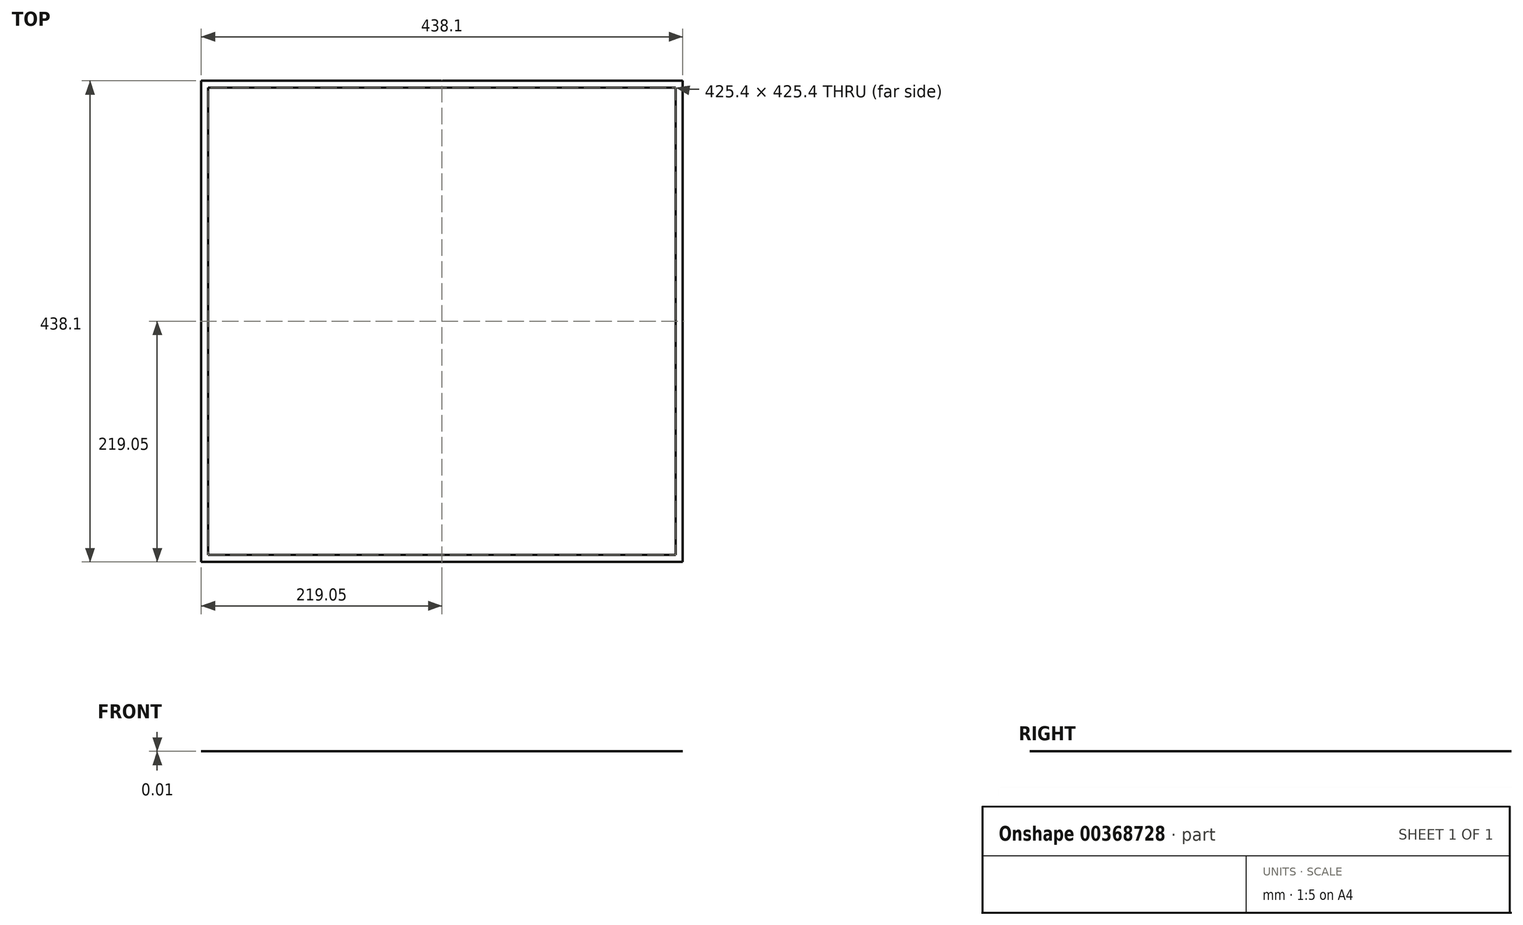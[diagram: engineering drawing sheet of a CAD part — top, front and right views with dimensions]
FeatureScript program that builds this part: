
annotation { "Feature Type Name" : "Feature", "Feature Type Description" : "" }
export const myFeature = defineFeature(function(context is Context, id is Id, definition is map)
    precondition{}
    {
        {
            var Q0;
            Q0=qCreatedBy(makeId("Top.planeOp"),FACE);
            var sketch = newSketch(context, id + "F0", { "sketchPlane" : qUnion([Q0])});
            skLineSegment(sketch, "E0.bottom", {"start": v(212.7, 212.7) * mm, "end": v(-212.7, 212.7) * mm});
            skLineSegment(sketch, "E0.top", {"start": v(212.7, -212.7) * mm, "end": v(-212.7, -212.7) * mm});
            skLineSegment(sketch, "E0.left", {"start": v(212.7, 212.7) * mm, "end": v(212.7, -212.7) * mm});
            skLineSegment(sketch, "E0.right", {"start": v(-212.7, 212.7) * mm, "end": v(-212.7, -212.7) * mm});
            skPoint(sketch, "E0.middle", {"position": v(0, 0) * mm});
            skLineSegment(sketch, "E1.bottom", {"start": v(219.05, 219.05) * mm, "end": v(-219.05, 219.05) * mm});
            skLineSegment(sketch, "E1.top", {"start": v(219.05, -219.05) * mm, "end": v(-219.05, -219.05) * mm});
            skLineSegment(sketch, "E1.left", {"start": v(219.05, 219.05) * mm, "end": v(219.05, -219.05) * mm});
            skLineSegment(sketch, "E1.right", {"start": v(-219.05, 219.05) * mm, "end": v(-219.05, -219.05) * mm});
            skSolve(sketch);
        }
        {
            var Q0;
            Q0=makeQuery(id+"F0.imprint","IMPRINT",FACE,{"disambiguationData":[TD([[makeQuery(id+"F0.imprint","IMPRINT",EDGE,{"derivedFrom":sQuery(id+"F0.wireOp",EDGE,"E0.bottom")}),-1.0]])]});
            extrude(context, id + "F1", {"entities" : qUnion([Q0]), "depth" : 1 / 101.6 * mm});
        }
    });
